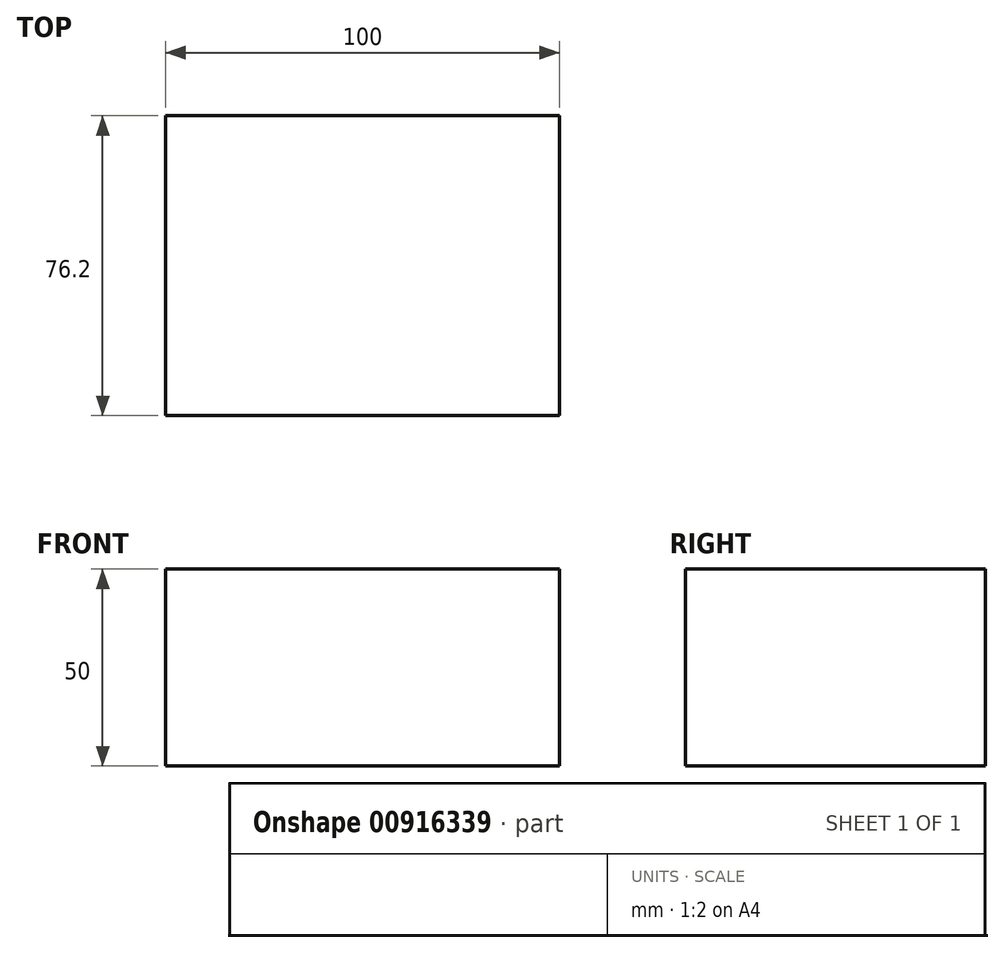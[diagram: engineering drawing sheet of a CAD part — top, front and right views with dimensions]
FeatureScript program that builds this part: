
annotation { "Feature Type Name" : "Feature", "Feature Type Description" : "" }
export const myFeature = defineFeature(function(context is Context, id is Id, definition is map)
    precondition{}
    {
        {
            var Q0;
            Q0=qCreatedBy(makeId("Front.planeOp"),FACE);
            var sketch = newSketch(context, id + "F0", { "sketchPlane" : qUnion([Q0])});
            skLineSegment(sketch, "E0.bottom", {"start": v(0, 0) * mm, "end": v(-100, 0) * mm});
            skLineSegment(sketch, "E0.top", {"start": v(0, 50) * mm, "end": v(-100, 50) * mm});
            skLineSegment(sketch, "E0.left", {"start": v(0, 0) * mm, "end": v(0, 50) * mm});
            skLineSegment(sketch, "E0.right", {"start": v(-100, 0) * mm, "end": v(-100, 50) * mm});
            skSolve(sketch);
        }
        {
            var Q0;
            Q0=makeQuery(id+"F0.imprint","IMPRINT",FACE,{"disambiguationData":[TD([[makeQuery(id+"F0.imprint","IMPRINT",EDGE,{"derivedFrom":sQuery(id+"F0.wireOp",EDGE,"E0.bottom")}),-1.0]])]});
            extrude(context, id + "F1", {"entities" : qUnion([Q0]), "depth" : 76.2 * mm, "offsetDistance" : 25.4 * mm});
        }
    });
